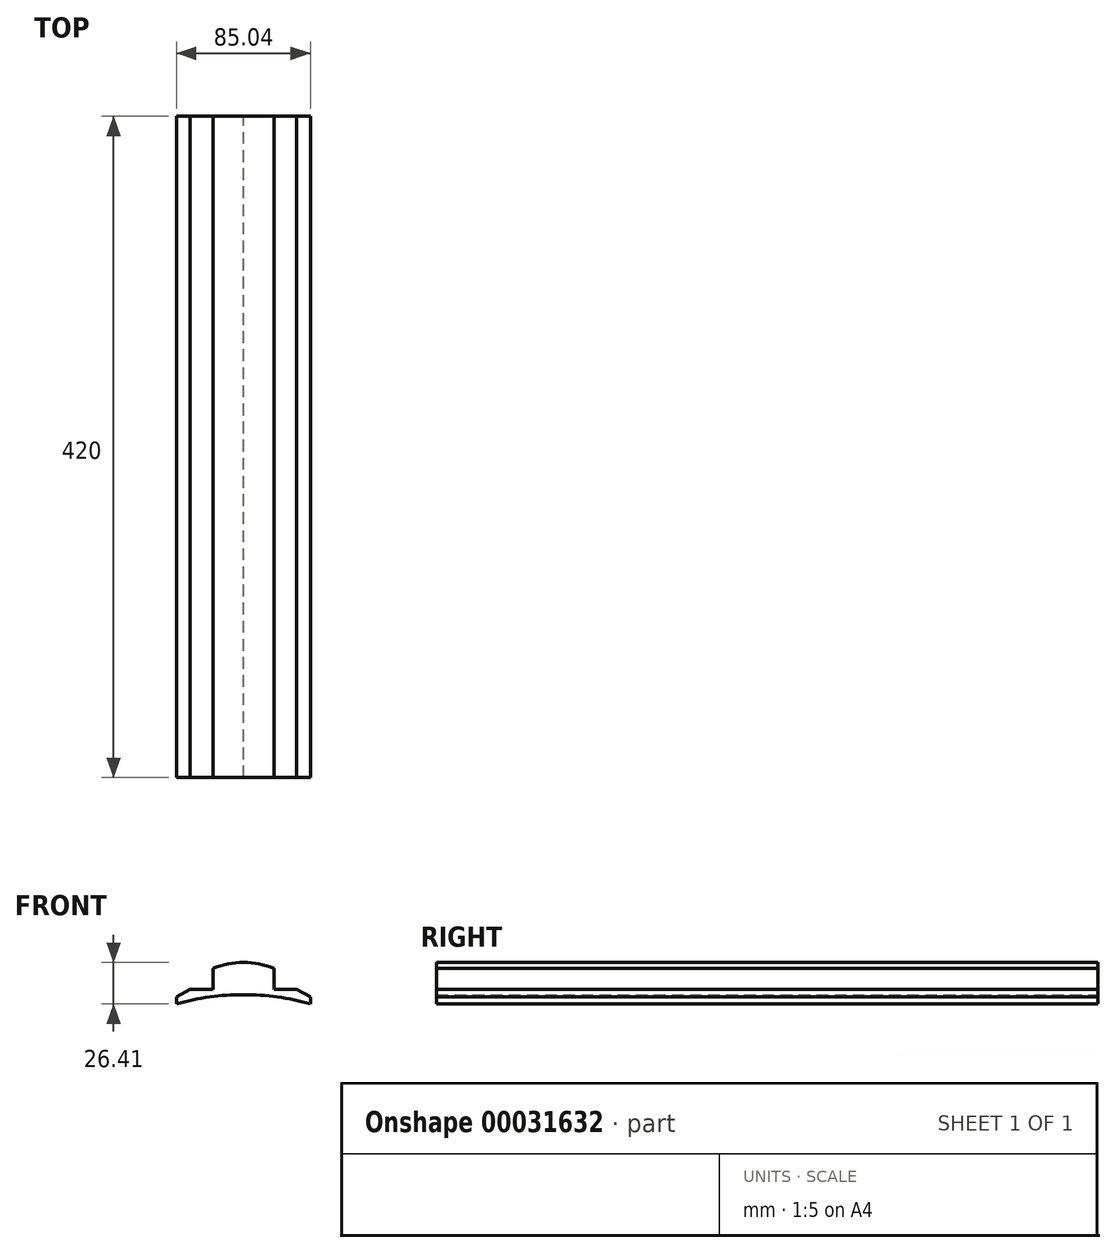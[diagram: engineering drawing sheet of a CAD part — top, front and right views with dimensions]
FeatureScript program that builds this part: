
annotation { "Feature Type Name" : "Feature", "Feature Type Description" : "" }
export const myFeature = defineFeature(function(context is Context, id is Id, definition is map)
    precondition{}
    {
        {
            var Q0;
            Q0=qCreatedBy(makeId("Front.planeOp"),FACE);
            var sketch = newSketch(context, id + "F0", { "sketchPlane" : qUnion([Q0])});
            skLineSegment(sketch, "E0", {"start": v(19.33, 30.44) * mm, "end": v(19.33, 17.23) * mm});
            skLineSegment(sketch, "E1", {"start": v(19.33, 17.23) * mm, "end": v(33.82, 17.23) * mm});
            skLineSegment(sketch, "E2", {"start": v(33.82, 17.23) * mm, "end": v(42.52, 12.4) * mm});
            skLineSegment(sketch, "E3", {"start": v(42.52, 12.4) * mm, "end": v(42.52, 7.9) * mm});
            skArc(sketch, "E4", {"start": v(42.52, 7.9) * mm, "mid": v(21.47, 12.37) * mm, "end": v(0, 13.69) * mm});
            skArc(sketch, "E5", {"start": v(19.33, 30.44) * mm, "mid": v(9.85, 33.33) * mm, "end": v(0, 34.3) * mm});
            skLineSegment(sketch, "E6", {"start": v(0, 0) * mm, "end": v(0, 44.6) * mm, "construction": true});
            skArc(sketch, "E7.MirrorCS", {"start": v(-19.33, 30.44) * mm, "mid": v(-9.85, 33.33) * mm, "end": v(0, 34.3) * mm});
            skLineSegment(sketch, "E8.MirrorCS", {"start": v(-19.33, 30.44) * mm, "end": v(-19.33, 17.23) * mm});
            skLineSegment(sketch, "E9.MirrorCS", {"start": v(-19.33, 17.23) * mm, "end": v(-33.82, 17.23) * mm});
            skLineSegment(sketch, "E10.MirrorCS", {"start": v(-33.82, 17.23) * mm, "end": v(-42.52, 12.4) * mm});
            skArc(sketch, "E11.MirrorCS", {"start": v(-42.52, 7.9) * mm, "mid": v(-21.47, 12.37) * mm, "end": v(0, 13.69) * mm});
            skLineSegment(sketch, "E12.MirrorCS", {"start": v(-42.52, 12.4) * mm, "end": v(-42.52, 7.9) * mm});
            skSolve(sketch);
        }
        {
            var Q0;
            Q0=makeQuery(id+"F0.imprint","IMPRINT",FACE,{"disambiguationData":[TD([[makeQuery(id+"F0.imprint","IMPRINT",EDGE,{"derivedFrom":sQuery(id+"F0.wireOp",EDGE,"E0")}),-1.0]])]});
            extrude(context, id + "F1", {"entities" : qUnion([Q0]), "depth" : 420 * mm});
        }
    });
